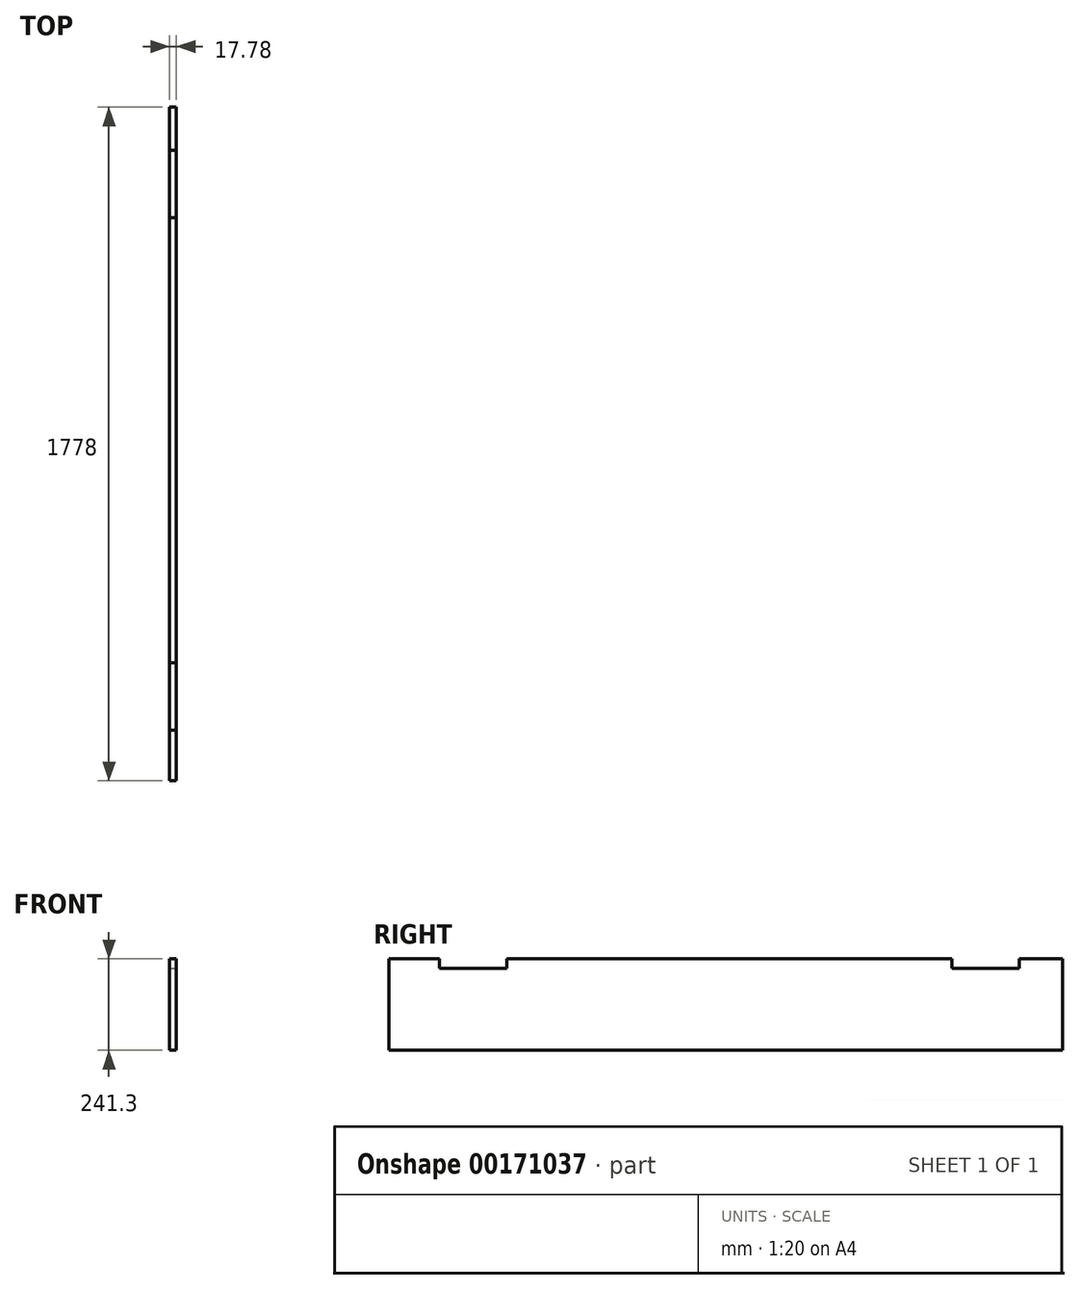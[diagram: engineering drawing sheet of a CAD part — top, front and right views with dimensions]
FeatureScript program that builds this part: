
annotation { "Feature Type Name" : "Feature", "Feature Type Description" : "" }
export const myFeature = defineFeature(function(context is Context, id is Id, definition is map)
    precondition{}
    {
        {
            var Q0;
            Q0=qCreatedBy(makeId("Front.planeOp"),FACE);
            var sketch = newSketch(context, id + "F0", { "sketchPlane" : qUnion([Q0])});
            skLineSegment(sketch, "E0.bottom", {"start": v(0, 0) * mm, "end": v(17.78, 0) * mm});
            skLineSegment(sketch, "E0.top", {"start": v(0, 241.3) * mm, "end": v(17.78, 241.3) * mm});
            skLineSegment(sketch, "E0.left", {"start": v(0, 0) * mm, "end": v(0, 241.3) * mm});
            skLineSegment(sketch, "E0.right", {"start": v(17.78, 0) * mm, "end": v(17.78, 241.3) * mm});
            skSolve(sketch);
        }
        {
            var Q0;
            Q0=makeQuery(id+"F0.imprint","IMPRINT",FACE,{"disambiguationData":[TD([[makeQuery(id+"F0.imprint","IMPRINT",EDGE,{"derivedFrom":sQuery(id+"F0.wireOp",EDGE,"E0.bottom")}),1.0]])]});
            extrude(context, id + "F1", {"entities" : qUnion([Q0]), "depth" : 1778 * mm});
        }
        {
            var Q0;
            Q0=makeQuery(id+"F1.opExtrude","SWEPT_FACE",FACE,{"disambiguationData":[OSD([sQuery(id+"F0.wireOp",EDGE,"E0.right")])]});
            var sketch = newSketch(context, id + "F2", { "sketchPlane" : qUnion([Q0])});
            skLineSegment(sketch, "E1.bottom", {"start": v(-114.3, 241.3) * mm, "end": v(-292.1, 241.3) * mm});
            skLineSegment(sketch, "E1.top", {"start": v(-114.3, 215.9) * mm, "end": v(-292.1, 215.9) * mm});
            skLineSegment(sketch, "E1.left", {"start": v(-114.3, 241.3) * mm, "end": v(-114.3, 215.9) * mm});
            skLineSegment(sketch, "E1.right", {"start": v(-292.1, 241.3) * mm, "end": v(-292.1, 215.9) * mm});
            skLineSegment(sketch, "E2.bottom", {"start": v(-1466.85, 241.3) * mm, "end": v(-1644.65, 241.3) * mm});
            skLineSegment(sketch, "E2.top", {"start": v(-1466.85, 215.9) * mm, "end": v(-1644.65, 215.9) * mm});
            skLineSegment(sketch, "E2.left", {"start": v(-1466.85, 241.3) * mm, "end": v(-1466.85, 215.9) * mm});
            skLineSegment(sketch, "E2.right", {"start": v(-1644.65, 241.3) * mm, "end": v(-1644.65, 215.9) * mm});
            skSolve(sketch);
        }
        {
            var Q0;
            Q0 = qSketchRegion(id + "F2", true);
            extrude(context, id + "F3", {"entities" : qUnion([Q0]), "operationType" : NewBodyOperationType.REMOVE, "endBound" : BoundingType.THROUGH_ALL, "oppositeDirection" : true, "depth" : 25.4 * mm});
        }
    });
